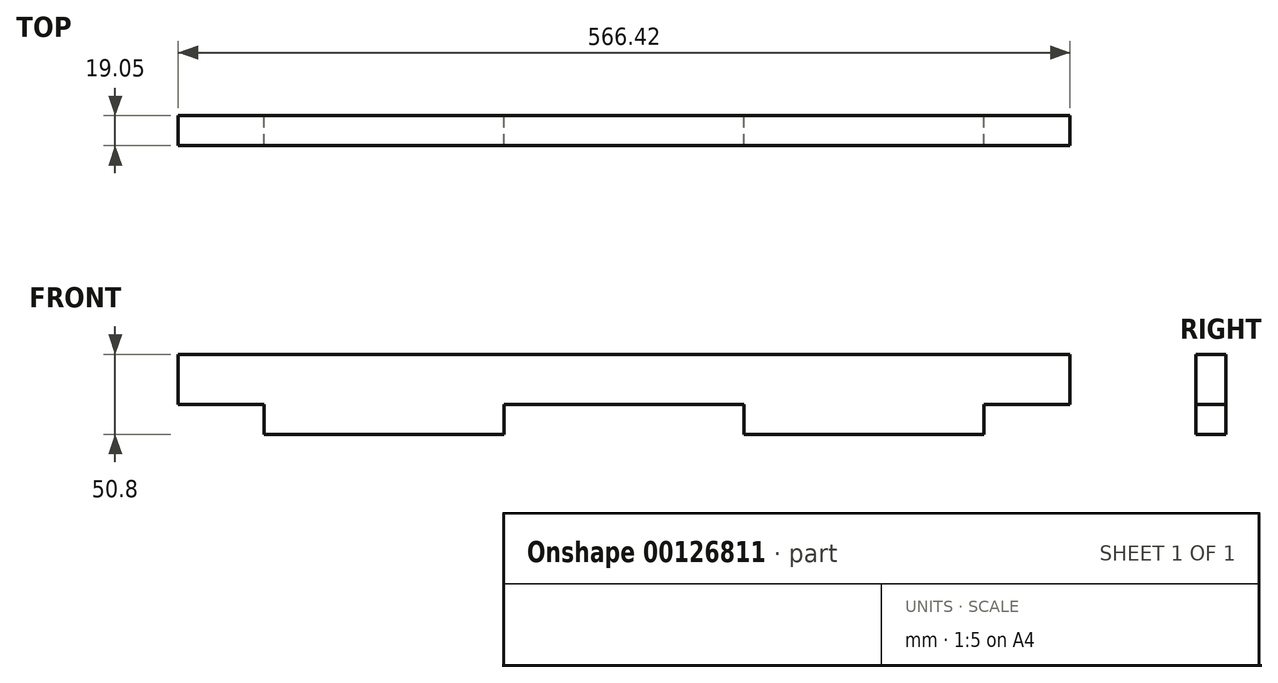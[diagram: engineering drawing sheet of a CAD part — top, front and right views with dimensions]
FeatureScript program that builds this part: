
annotation { "Feature Type Name" : "Feature", "Feature Type Description" : "" }
export const myFeature = defineFeature(function(context is Context, id is Id, definition is map)
    precondition{}
    {
        {
            var Q0;
            Q0=qCreatedBy(makeId("Front.planeOp"),FACE);
            var sketch = newSketch(context, id + "F0", { "sketchPlane" : qUnion([Q0])});
            skLineSegment(sketch, "E0", {"start": v(-317.1, 25.42) * mm, "end": v(-262.5, 25.42) * mm});
            skLineSegment(sketch, "E1", {"start": v(-262.5, 25.42) * mm, "end": v(-262.5, 6.37) * mm});
            skLineSegment(sketch, "E2", {"start": v(-262.5, 6.37) * mm, "end": v(-110.1, 6.37) * mm});
            skLineSegment(sketch, "E3", {"start": v(-110.1, 6.37) * mm, "end": v(-110.1, 25.42) * mm});
            skLineSegment(sketch, "E4", {"start": v(-110.1, 25.42) * mm, "end": v(42.3, 25.42) * mm});
            skLineSegment(sketch, "E5", {"start": v(42.3, 25.42) * mm, "end": v(42.3, 6.37) * mm});
            skLineSegment(sketch, "E6", {"start": v(42.3, 6.37) * mm, "end": v(194.7, 6.37) * mm});
            skLineSegment(sketch, "E7", {"start": v(194.7, 6.37) * mm, "end": v(194.7, 25.42) * mm});
            skLineSegment(sketch, "E8", {"start": v(194.7, 25.42) * mm, "end": v(249.32, 25.42) * mm});
            skLineSegment(sketch, "E9", {"start": v(-317.1, 25.42) * mm, "end": v(-317.1, 57.17) * mm});
            skLineSegment(sketch, "E10", {"start": v(-317.1, 57.17) * mm, "end": v(249.32, 57.17) * mm});
            skLineSegment(sketch, "E11", {"start": v(249.32, 57.17) * mm, "end": v(249.32, 25.42) * mm});
            skSolve(sketch);
        }
        {
            var Q0;
            Q0 = qSketchRegion(id + "F0", true);
            extrude(context, id + "F1", {"entities" : qUnion([Q0]), "depth" : 19.05 * mm});
        }
    });
